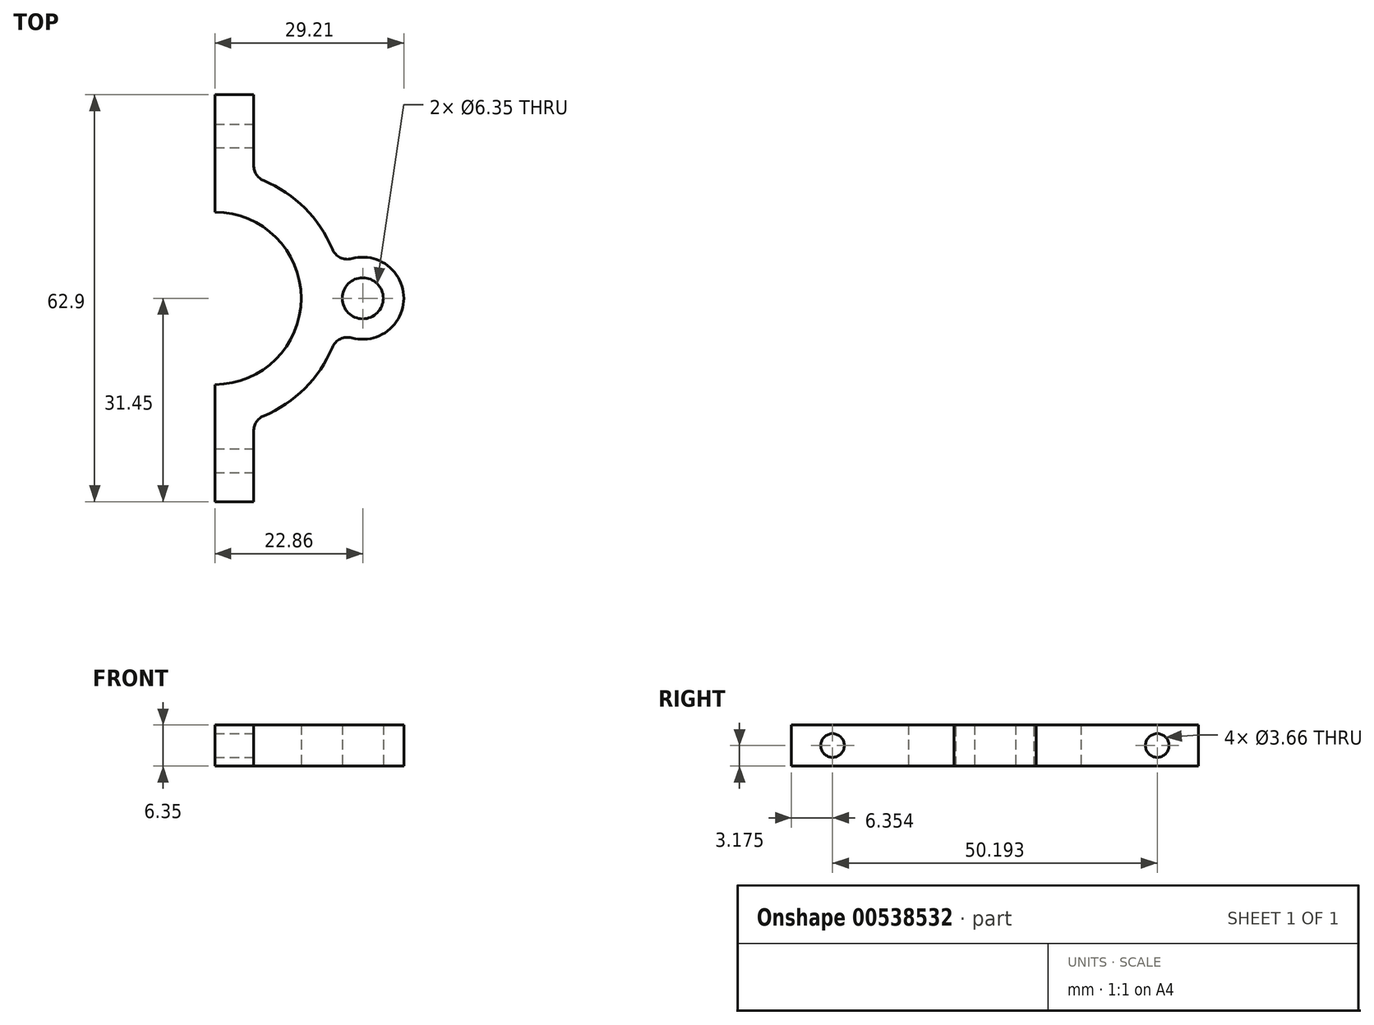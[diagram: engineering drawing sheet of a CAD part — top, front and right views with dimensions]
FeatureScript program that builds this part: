
annotation { "Feature Type Name" : "Feature", "Feature Type Description" : "" }
export const myFeature = defineFeature(function(context is Context, id is Id, definition is map)
    precondition{}
    {
        {
            var Q0;
            Q0=qCreatedBy(makeId("Top.planeOp"),FACE);
            var sketch = newSketch(context, id + "F0", { "sketchPlane" : qUnion([Q0])});
            skArc(sketch, "E0", {"start": v(0, -13.34) * mm, "mid": v(13.34, 0) * mm, "end": v(0, 13.34) * mm});
            skArc(sketch, "E1", {"start": v(6, -18.75) * mm, "mid": v(14.26, -13.57) * mm, "end": v(19.02, -5.06) * mm});
            skLineSegment(sketch, "E2.bottom", {"start": v(6, -31.45) * mm, "end": v(0, -31.45) * mm});
            skLineSegment(sketch, "E2.top", {"start": v(6, 31.45) * mm, "end": v(0, 31.45) * mm});
            skLineSegment(sketch, "E2.left", {"start": v(6, -31.45) * mm, "end": v(6, -18.75) * mm});
            skLineSegment(sketch, "E3", {"start": v(0, 31.45) * mm, "end": v(0, 13.34) * mm});
            skLineSegment(sketch, "E4.trimOffspring", {"start": v(6, 18.75) * mm, "end": v(6, 31.45) * mm});
            skPoint(sketch, "E5.orphan", {"position": v(-6, -31.45) * mm});
            skPoint(sketch, "E6.orphan", {"position": v(-6, 31.45) * mm});
            skLineSegment(sketch, "E7.trimOffspring", {"start": v(0, -13.34) * mm, "end": v(0, -31.45) * mm});
            skCircle(sketch, "E8", {"center": v(22.86, 0) * mm, "radius": 3.18 * mm});
            skArc(sketch, "E9", {"start": v(19.02, -5.06) * mm, "mid": v(29.21, 0) * mm, "end": v(19.02, 5.06) * mm});
            skLineSegment(sketch, "E10", {"start": v(19.69, 0) * mm, "end": v(13.34, 0) * mm, "construction": true});
            skPoint(sketch, "E11", {"position": v(16.51, 0) * mm});
            skArc(sketch, "E12.trimOffspring", {"start": v(19.02, 5.06) * mm, "mid": v(14.26, 13.57) * mm, "end": v(6, 18.75) * mm});
            skSolve(sketch);
        }
        {
            var Q0;
            Q0=makeQuery(id+"F0.imprint","IMPRINT",FACE,{"disambiguationData":[TD([[makeQuery(id+"F0.imprint","IMPRINT",EDGE,{"derivedFrom":sQuery(id+"F0.wireOp",EDGE,"E0")}),-1.0]])]});
            extrude(context, id + "F1", {"entities" : qUnion([Q0]), "depth" : 6.35 * mm, "offsetDistance" : 25.4 * mm});
        }
        {
            var Q0;
            Q0=makeQuery(id+"F1.opExtrude","SWEPT_FACE",FACE,{"disambiguationData":[OSD([sQuery(id+"F0.wireOp",EDGE,"E2.left")])]});
            var sketch = newSketch(context, id + "F2", { "sketchPlane" : qUnion([Q0])});
            skLineSegment(sketch, "E13", {"start": v(-25.1, 0) * mm, "end": v(-25.1, 6.35) * mm, "construction": true});
            skLineSegment(sketch, "E14", {"start": v(-31.45, 3.18) * mm, "end": v(-18.75, 3.18) * mm, "construction": true});
            skCircle(sketch, "E15", {"center": v(-25.1, 3.18) * mm, "radius": 1.83 * mm});
            skSolve(sketch);
        }
        {
            var Q0;
            Q0=makeQuery(id+"F1.opExtrude","SWEPT_FACE",FACE,{"disambiguationData":[OSD([sQuery(id+"F0.wireOp",EDGE,"E4.trimOffspring")])]});
            var sketch = newSketch(context, id + "F3", { "sketchPlane" : qUnion([Q0])});
            skLineSegment(sketch, "E16", {"start": v(25.1, 6.35) * mm, "end": v(25.1, 0) * mm, "construction": true});
            skLineSegment(sketch, "E17", {"start": v(18.75, 3.18) * mm, "end": v(31.45, 3.18) * mm, "construction": true});
            skCircle(sketch, "E18", {"center": v(25.1, 3.18) * mm, "radius": 1.83 * mm});
            skSolve(sketch);
        }
        {
            var Q0;
            Q0=makeQuery(id+"F2.imprint","IMPRINT",FACE,{"disambiguationData":[TD([[makeQuery(id+"F2.imprint","IMPRINT",EDGE,{"derivedFrom":sQuery(id+"F2.wireOp",EDGE,"E15")}),1.0]])]});
            var Q1;
            Q1=makeQuery(id+"F3.imprint","IMPRINT",FACE,{"disambiguationData":[TD([[makeQuery(id+"F3.imprint","IMPRINT",EDGE,{"derivedFrom":sQuery(id+"F3.wireOp",EDGE,"E18")}),1.0]])]});
            var Q2;
            Q2=makeQuery(id+"F1.opExtrude","SWEPT_FACE",FACE,{"disambiguationData":[OSD([sQuery(id+"F0.wireOp",EDGE,"E3")])]});
            extrude(context, id + "F4", {"entities" : qUnion([Q0, Q1]), "operationType" : NewBodyOperationType.REMOVE, "endBound" : BoundingType.UP_TO_SURFACE, "oppositeDirection" : true, "depth" : 25.4 * mm, "endBoundEntityFace" : qUnion([Q2]), "offsetDistance" : 25.4 * mm});
        }
        {
            var Q0;
            Q0=makeQuery(id+"F1.opExtrude","SWEPT_EDGE",EDGE,{"disambiguationData":[OSD([sQuery(id+"F0.wireOp",EDGE,"E9"),sQuery(id+"F0.wireOp",EDGE,"E12.trimOffspring")])]});
            var Q1;
            Q1=makeQuery(id+"F1.opExtrude","SWEPT_EDGE",EDGE,{"disambiguationData":[OSD([sQuery(id+"F0.wireOp",EDGE,"E1"),sQuery(id+"F0.wireOp",EDGE,"E9")])]});
            var Q2;
            Q2=makeQuery(id+"F1.opExtrude","SWEPT_EDGE",EDGE,{"disambiguationData":[OSD([sQuery(id+"F0.wireOp",EDGE,"E1"),sQuery(id+"F0.wireOp",EDGE,"E2.left")])]});
            var Q3;
            Q3=makeQuery(id+"F1.opExtrude","SWEPT_EDGE",EDGE,{"disambiguationData":[OSD([sQuery(id+"F0.wireOp",EDGE,"E4.trimOffspring"),sQuery(id+"F0.wireOp",EDGE,"E12.trimOffspring")])]});
            fillet(context, id + "F5", {"entities" : qUnion([Q0, Q1, Q2, Q3]), "radius" : 2.54 * mm, "tangentPropagation" : true, "allowEdgeOverflow" : false});
        }
    });
